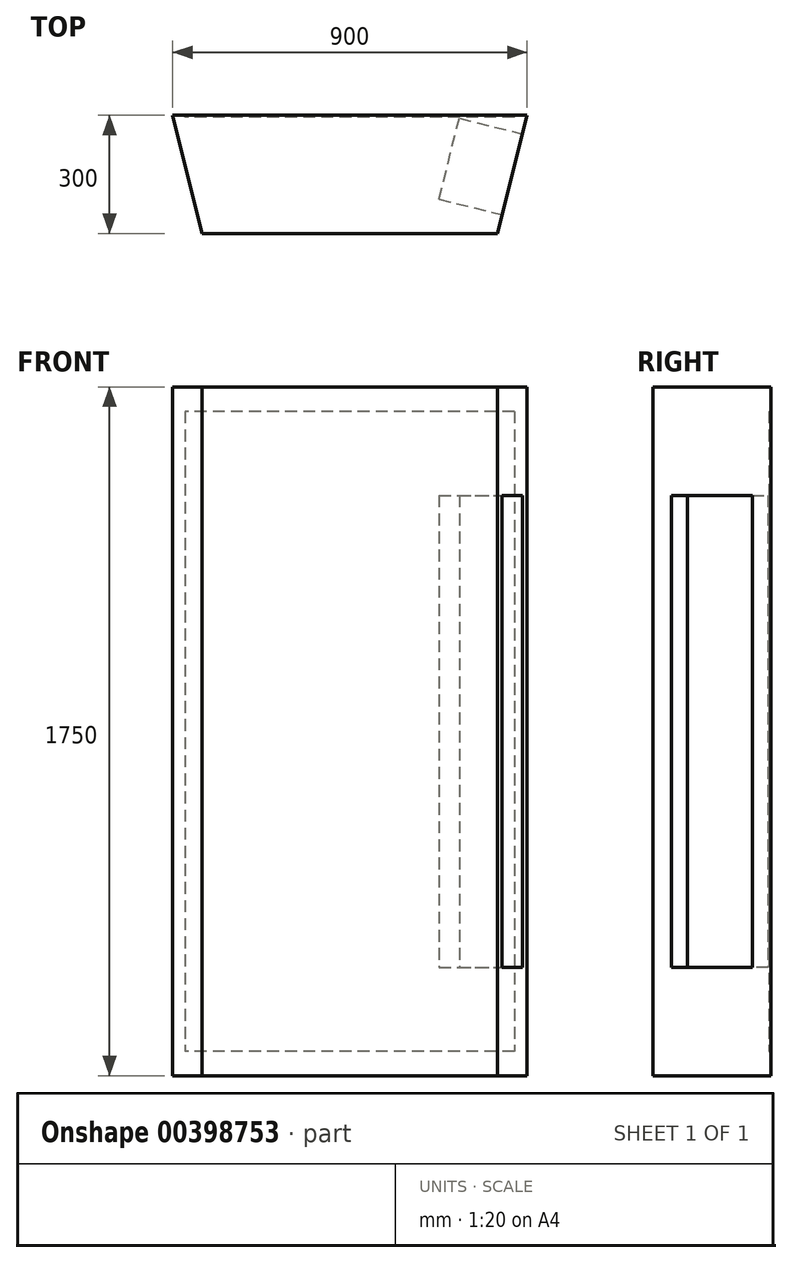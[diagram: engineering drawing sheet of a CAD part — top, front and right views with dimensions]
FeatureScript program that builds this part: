
annotation { "Feature Type Name" : "Feature", "Feature Type Description" : "" }
export const myFeature = defineFeature(function(context is Context, id is Id, definition is map)
    precondition{}
    {
        {
            var Q0;
            Q0=qCreatedBy(makeId("Top.planeOp"),FACE);
            var sketch = newSketch(context, id + "F0", { "sketchPlane" : qUnion([Q0])});
            skLineSegment(sketch, "E0", {"start": v(-413.97, -94.03) * mm, "end": v(336.03, -94.03) * mm});
            skPoint(sketch, "E1.orphan", {"position": v(-413.97, 205.97) * mm});
            skPoint(sketch, "E2.end.orphan", {"position": v(336.03, 205.97) * mm});
            skLineSegment(sketch, "E3", {"start": v(-38.97, 205.97) * mm, "end": v(-488.97, 205.97) * mm});
            skLineSegment(sketch, "E4", {"start": v(-38.97, 205.97) * mm, "end": v(411.03, 205.97) * mm});
            skLineSegment(sketch, "E5", {"start": v(336.03, -94.03) * mm, "end": v(411.03, 205.97) * mm});
            skLineSegment(sketch, "E6", {"start": v(-488.97, 205.97) * mm, "end": v(-413.97, -94.03) * mm});
            skSolve(sketch);
        }
        {
            var Q0;
            Q0=makeQuery(id+"F0.imprint","IMPRINT",FACE,{"disambiguationData":[TD([[makeQuery(id+"F0.imprint","IMPRINT",EDGE,{"derivedFrom":sQuery(id+"F0.wireOp",EDGE,"E0")}),1.0]])]});
            extrude(context, id + "F1", {"entities" : qUnion([Q0]), "depth" : 1750 * mm});
        }
        {
            var Q0;
            Q0=makeQuery(id+"F1.opExtrude","SWEPT_FACE",FACE,{"disambiguationData":[OSD([sQuery(id+"F0.wireOp",EDGE,"E3"),sQuery(id+"F0.wireOp",EDGE,"E4")])]});
            var sketch = newSketch(context, id + "F2", { "sketchPlane" : qUnion([Q0])});
            skLineSegment(sketch, "E7.bottom", {"start": v(-379.02, 1687.75) * mm, "end": v(456.95, 1687.75) * mm});
            skLineSegment(sketch, "E7.top", {"start": v(-379.02, 62.25) * mm, "end": v(456.95, 62.25) * mm});
            skLineSegment(sketch, "E7.left", {"start": v(-379.02, 1687.75) * mm, "end": v(-379.02, 62.25) * mm});
            skLineSegment(sketch, "E7.right", {"start": v(456.95, 1687.75) * mm, "end": v(456.95, 62.25) * mm});
            skSolve(sketch);
        }
        {
            var Q0;
            Q0=makeQuery(id+"F2.imprint","IMPRINT",FACE,{"disambiguationData":[TD([[makeQuery(id+"F2.imprint","IMPRINT",EDGE,{"derivedFrom":sQuery(id+"F2.wireOp",EDGE,"E7.bottom")}),-1.0]])]});
            extrude(context, id + "F3", {"entities" : qUnion([Q0]), "operationType" : NewBodyOperationType.REMOVE, "oppositeDirection" : true, "depth" : 5 * mm});
        }
        {
            var Q0;
            Q0=makeQuery(id+"F1.opExtrude","SWEPT_FACE",FACE,{"disambiguationData":[OSD([sQuery(id+"F0.wireOp",EDGE,"E5")])]});
            var sketch = newSketch(context, id + "F4", { "sketchPlane" : qUnion([Q0])});
            skLineSegment(sketch, "E8.bottom", {"start": v(39, 1474.27) * mm, "end": v(250.79, 1474.27) * mm});
            skLineSegment(sketch, "E8.top", {"start": v(39, 275.73) * mm, "end": v(250.79, 275.73) * mm});
            skLineSegment(sketch, "E8.left", {"start": v(39, 1474.27) * mm, "end": v(39, 275.73) * mm});
            skLineSegment(sketch, "E8.right", {"start": v(250.79, 1474.27) * mm, "end": v(250.79, 275.73) * mm});
            skSolve(sketch);
        }
        {
            var Q0;
            Q0=makeQuery(id+"F4.imprint","IMPRINT",FACE,{"disambiguationData":[TD([[makeQuery(id+"F4.imprint","IMPRINT",EDGE,{"derivedFrom":sQuery(id+"F4.wireOp",EDGE,"E8.bottom")}),-1.0]])]});
            extrude(context, id + "F5", {"entities" : qUnion([Q0]), "operationType" : NewBodyOperationType.REMOVE, "oppositeDirection" : true, "depth" : 165 * mm});
        }
    });
